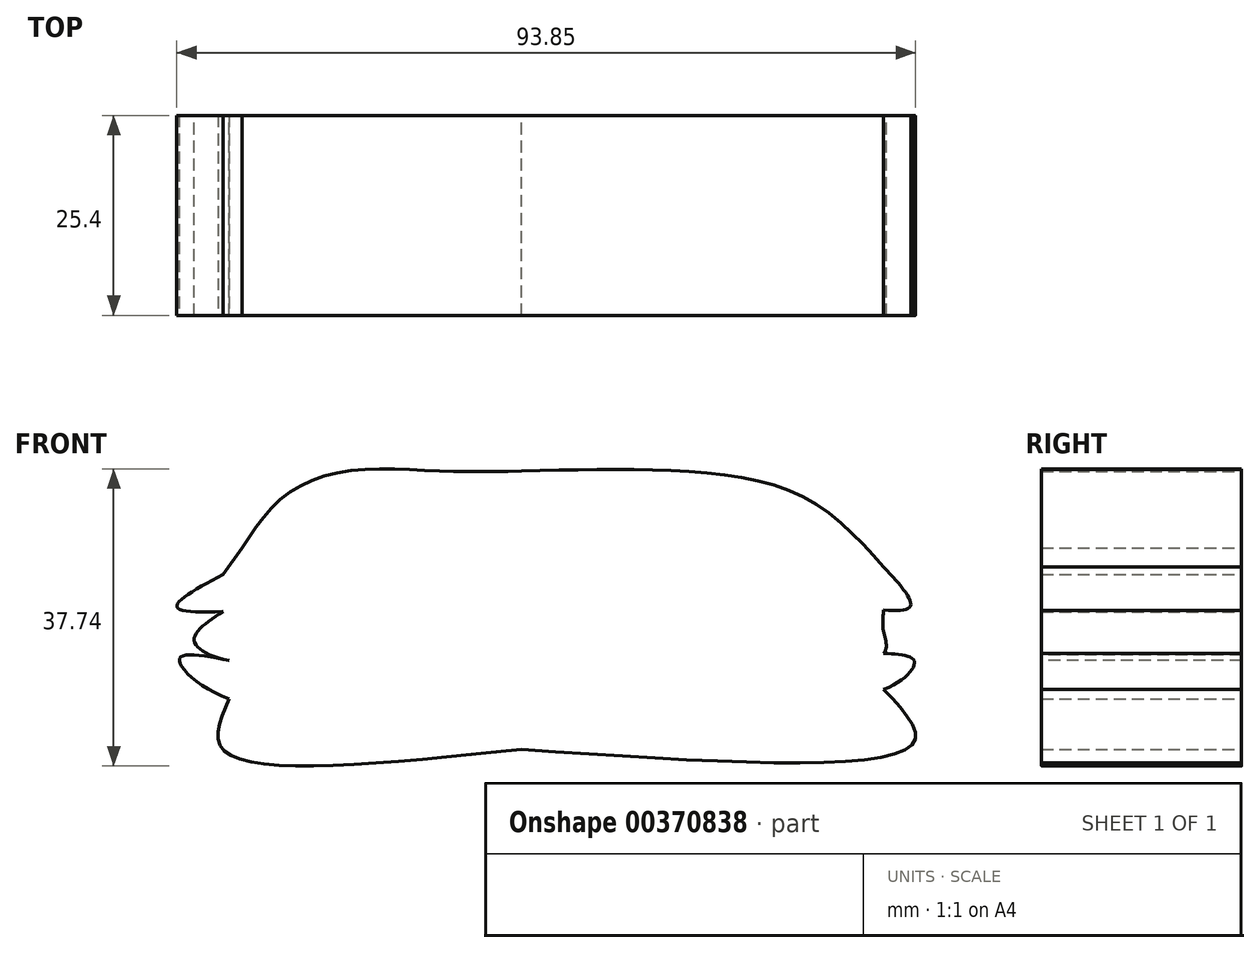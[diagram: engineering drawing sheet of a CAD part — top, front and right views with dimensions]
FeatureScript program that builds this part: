
annotation { "Feature Type Name" : "Feature", "Feature Type Description" : "" }
export const myFeature = defineFeature(function(context is Context, id is Id, definition is map)
    precondition{}
    {
        {
            var Q0;
            Q0=qCreatedBy(makeId("Front.planeOp"),FACE);
            var sketch = newSketch(context, id + "F0", { "sketchPlane" : qUnion([Q0])});
            skLineSegment(sketch, "E0", {"start": v(0, -42.52) * mm, "end": v(0, 59.9) * mm, "construction": true});
            skFitSpline(sketch, "E1", {"points": [v(0, 59.9) * mm, v(20.12, 59.9) * mm, v(35.97, 56.54) * mm, v(46.02, 47.7) * mm], "startDerivative": vector(55.39, 1.43) * mm, "endDerivative": vector(30.18, -33.68) * mm});
            skLineSegment(sketch, "E2", {"start": v(46.02, 47.7) * mm, "end": v(0, 47.7) * mm});
            skFitSpline(sketch, "E3", {"points": [v(0, 43.74) * mm, v(9.04, 43.43) * mm, v(22.45, 39.47) * mm, v(22.75, 39.47) * mm, v(30.68, 43.13) * mm, v(49.27, 42.52) * mm, v(46.02, 47.7) * mm], "startDerivative": vector(42.73, 4.14) * mm, "endDerivative": vector(-42.54, 45.54) * mm});
            skFitSpline(sketch, "E4", {"points": [v(0, 38.56) * mm, v(22.75, 36.73) * mm, v(46.02, 36.73) * mm, v(46.02, 39.47) * mm, v(46.02, 42.23) * mm], "startDerivative": vector(54.71, -4.04) * mm, "endDerivative": vector(2.29, 20.75) * mm});
            skFitSpline(sketch, "E5", {"points": [v(0, 33.38) * mm, v(46.02, 32.16) * mm, v(49.88, 35.81) * mm, v(46.02, 36.73) * mm], "startDerivative": vector(92.9, -10.85) * mm, "endDerivative": vector(-29.33, 1.5) * mm});
            skFitSpline(sketch, "E6", {"points": [v(46.02, 32.16) * mm, v(49.88, 25.45) * mm, v(0, 24.54) * mm], "startDerivative": vector(25.4, -26.9) * mm, "endDerivative": vector(-99.36, 6.78) * mm});
            skFitSpline(sketch, "E7", {"points": [v(0, 59.9) * mm, v(-10.17, 59.9) * mm, v(-22.05, 59.9) * mm, v(-30.28, 56.54) * mm, v(-35.46, 50.14) * mm], "startDerivative": vector(-38.56, -0.78) * mm, "endDerivative": vector(-20.04, -30.55) * mm});
            skFitSpline(sketch, "E8", {"points": [v(-35.46, 50.14) * mm, v(-37.9, 46.79) * mm], "startDerivative": vector(-2.44, -3.35) * mm, "endDerivative": vector(-2.44, -3.35) * mm});
            skLineSegment(sketch, "E9", {"start": v(-37.9, 46.79) * mm, "end": v(0, 47.7) * mm});
            skFitSpline(sketch, "E10", {"points": [v(-37.9, 46.79) * mm, v(-43.7, 42.52) * mm, v(-18.1, 43.74) * mm, v(0, 43.74) * mm], "startDerivative": vector(-42.86, -23.41) * mm, "endDerivative": vector(41.53, -2.52) * mm});
            skFitSpline(sketch, "E11", {"points": [v(-37.9, 42.06) * mm, v(-41.56, 38.56) * mm, v(-37.09, 35.81) * mm, v(0, 38.56) * mm], "startDerivative": vector(-25.52, -16.94) * mm, "endDerivative": vector(77.64, 11.02) * mm});
            skFitSpline(sketch, "E12", {"points": [v(0, 33.38) * mm, v(-37.09, 30.94) * mm, v(-43.39, 36.12) * mm, v(-37.09, 35.81) * mm], "startDerivative": vector(-80.44, -15.71) * mm, "endDerivative": vector(40.23, -7.8) * mm});
            skFitSpline(sketch, "E13", {"points": [v(0, 24.54) * mm, v(-37.9, 24.54) * mm, v(-37.09, 30.94) * mm], "startDerivative": vector(-73.48, -7.76) * mm, "endDerivative": vector(11, 25.11) * mm});
            skSolve(sketch);
        }
        {
            var Q0;
            Q0 = qSketchRegion(id + "F0", true);
            extrude(context, id + "F1", {"entities" : qUnion([Q0]), "depth" : 25.4 * mm});
        }
    });
